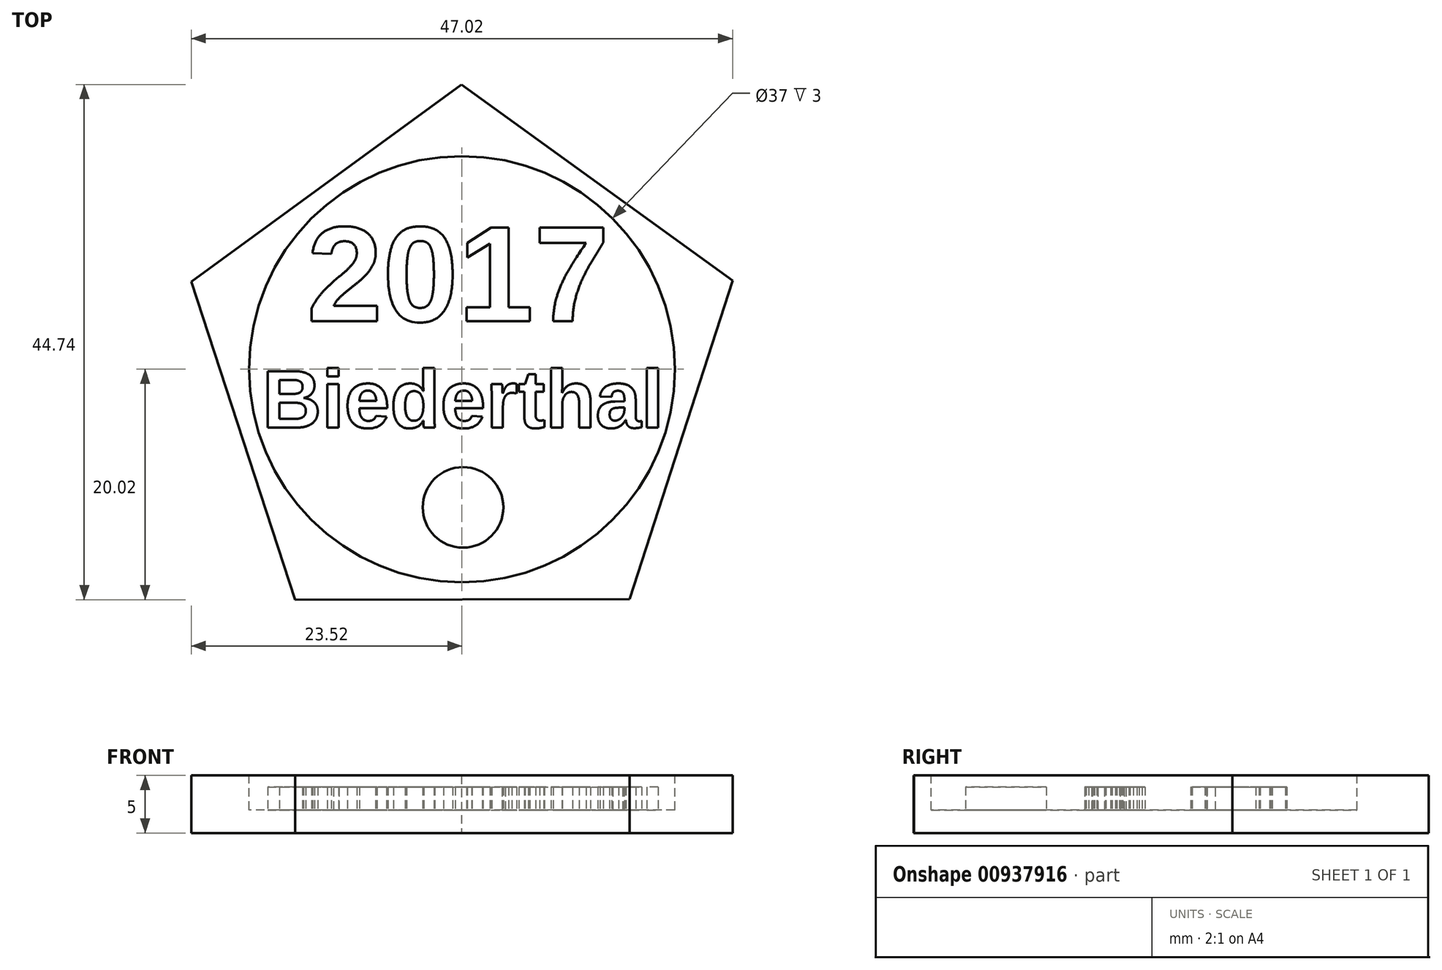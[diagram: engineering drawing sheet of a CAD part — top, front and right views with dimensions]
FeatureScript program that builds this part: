
annotation { "Feature Type Name" : "Feature", "Feature Type Description" : "" }
export const myFeature = defineFeature(function(context is Context, id is Id, definition is map)
    precondition{}
    {
        {
            var Q0;
            Q0=qCreatedBy(makeId("Top.planeOp"),FACE);
            var sketch = newSketch(context, id + "F0", { "sketchPlane" : qUnion([Q0])});
            skCircle(sketch, "E0.cCircle", {"center": v(0, 0) * mm, "radius": 20 * mm, "construction": true});
            skLineSegment(sketch, "E0.0", {"start": v(-23.52, 7.6) * mm, "end": v(-0.04, 24.72) * mm});
            skLineSegment(sketch, "E0.1", {"start": v(-0.04, 24.72) * mm, "end": v(23.5, 7.68) * mm});
            skLineSegment(sketch, "E0.2", {"start": v(23.5, 7.68) * mm, "end": v(14.56, -19.98) * mm});
            skLineSegment(sketch, "E0.3", {"start": v(14.56, -19.98) * mm, "end": v(-14.5, -20.02) * mm});
            skLineSegment(sketch, "E0.4", {"start": v(-14.5, -20.02) * mm, "end": v(-23.52, 7.6) * mm});
            skPoint(sketch, "E0.0.midPoint", {"position": v(-11.78, 16.16) * mm});
            skSolve(sketch);
        }
        {
            var Q0;
            Q0=qSketchRegion(id+"F0",true);
            extrude(context, id + "F1", {"entities" : qUnion([Q0]), "depth" : 5 * mm, "offsetDistance" : 25 * mm});
        }
        {
            var Q0;
            Q0=makeQuery(id+"F1.opExtrude","CAP_FACE",FACE,{"disambiguationData":[OSD([sQuery(id+"F0.wireOp",EDGE,"E0.0"),sQuery(id+"F0.wireOp",EDGE,"E0.1"),sQuery(id+"F0.wireOp",EDGE,"E0.2"),sQuery(id+"F0.wireOp",EDGE,"E0.3"),sQuery(id+"F0.wireOp",EDGE,"E0.4")])],"isStart":false});
            var sketch = newSketch(context, id + "F2", { "sketchPlane" : qUnion([Q0])});
            skCircle(sketch, "E1", {"center": v(0, 0) * mm, "radius": 18.5 * mm});
            skSolve(sketch);
        }
        {
            var Q0;
            {var subQ0=sQuery(id+"F2.wireOp",EDGE,"E1");var subQ4=makeQuery(id+"F2.imprint","INTERSECT",VERTEX,{"derivedFrom":[makeQuery(id+"F1.opExtrude","CAP_EDGE",EDGE,{"disambiguationData":[OSD([sQuery(id+"F0.wireOp",EDGE,"E0.0")])],"isStart":false}),subQ0]});Q0=makeQuery(id+"F2.imprint","IMPRINT",FACE,{"disambiguationData":[TD([[makeQuery(id+"F2.imprint","IMPRINT",EDGE,{"disambiguationData":[TD([[subQ4,1.0]])],"derivedFrom":subQ0}),1.0]])]});}
            extrude(context, id + "F3", {"entities" : qUnion([Q0]), "operationType" : NewBodyOperationType.REMOVE, "oppositeDirection" : true, "depth" : 3 * mm, "offsetDistance" : 25 * mm});
        }
        {
            var Q0;
            Q0=makeQuery(id+"F3.boolean.opBoolean","COPY",FACE,{"derivedFrom":makeQuery(id+"F3.opExtrude","CAP_FACE",FACE,{"disambiguationData":[OSD([sQuery(id+"F2.wireOp",EDGE,"E1")])],"isStart":false})});
            var sketch = newSketch(context, id + "F4", { "sketchPlane" : qUnion([Q0])});
            skText(sketch, "E2", { "text": "2017", "fontName": "Arimo-Bold.ttf"});
            skText(sketch, "E3", { "text": "Biederthal", "fontName": "Arimo-Bold.ttf"});
            skCircle(sketch, "E4", {"center": v(0.1, -12) * mm, "radius": 3.5 * mm});
            const initialGuessF4  = {"E2": [-0.01346, 0.00416, 1, 0, 0.0085], "E3": [-0.01736, -0.00508, 1, 0, 0.00514]};
            skSetInitialGuess(sketch, initialGuessF4);
            skSolve(sketch);
        }
        {
            var Q0;
            Q0=qSketchRegion(id+"F4",true);
            extrude(context, id + "F5", {"entities" : qUnion([Q0]), "operationType" : NewBodyOperationType.ADD, "depth" : 2 * mm, "offsetDistance" : 25 * mm});
        }
    });
